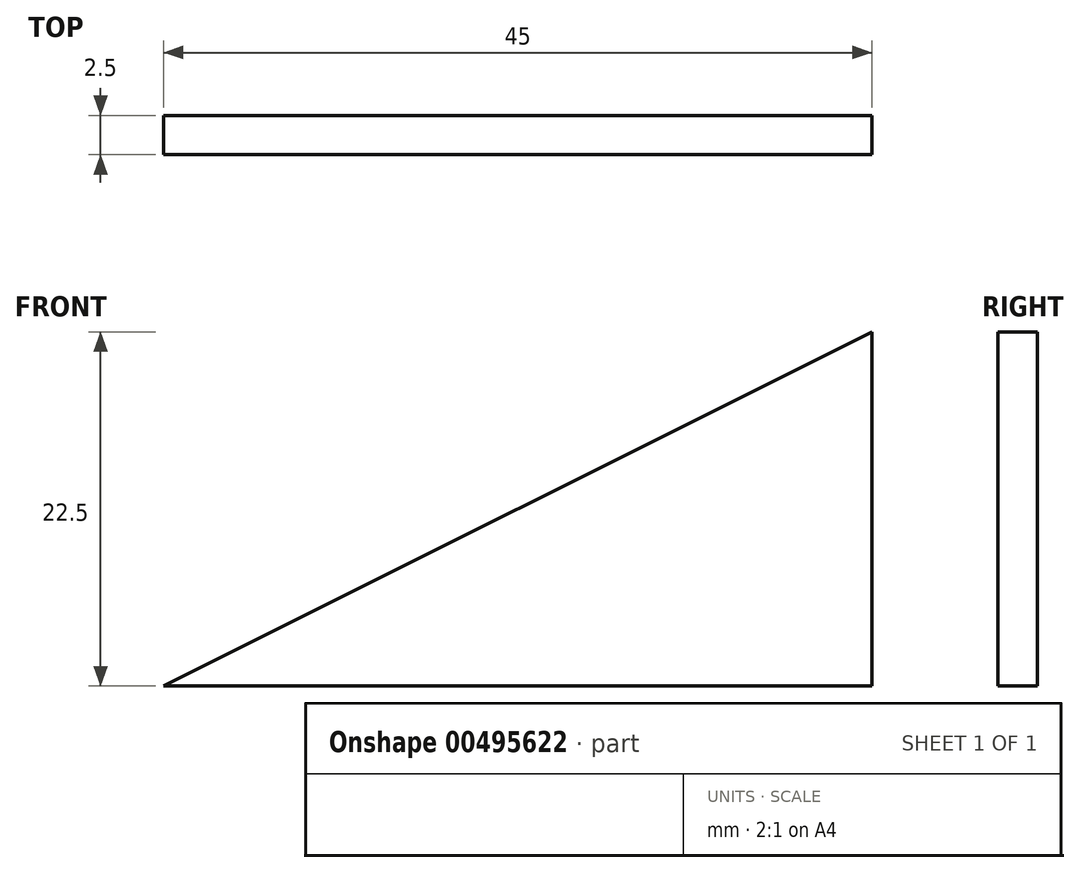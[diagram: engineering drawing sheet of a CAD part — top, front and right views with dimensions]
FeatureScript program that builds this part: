
annotation { "Feature Type Name" : "Feature", "Feature Type Description" : "" }
export const myFeature = defineFeature(function(context is Context, id is Id, definition is map)
    precondition{}
    {
        {
            var Q0;
            Q0=qCreatedBy(makeId("Front.planeOp"),FACE);
            var sketch = newSketch(context, id + "F0", { "sketchPlane" : qUnion([Q0])});
            skLineSegment(sketch, "E0.bottom", {"start": v(-56.54, 8.45) * mm, "end": v(-11.54, 8.45) * mm});
            skLineSegment(sketch, "E0.right", {"start": v(-11.54, 8.45) * mm, "end": v(-11.54, 30.95) * mm});
            skLineSegment(sketch, "E1", {"start": v(-56.54, 8.45) * mm, "end": v(-11.54, 30.95) * mm});
            skSolve(sketch);
        }
        {
            var Q0;
            Q0=makeQuery(id+"F0.imprint","IMPRINT",FACE,{"disambiguationData":[TD([[makeQuery(id+"F0.imprint","IMPRINT",EDGE,{"derivedFrom":sQuery(id+"F0.wireOp",EDGE,"E0.bottom")}),1.0]])]});
            extrude(context, id + "F1", {"entities" : qUnion([Q0]), "depth" : 2.5 * mm});
        }
    });
